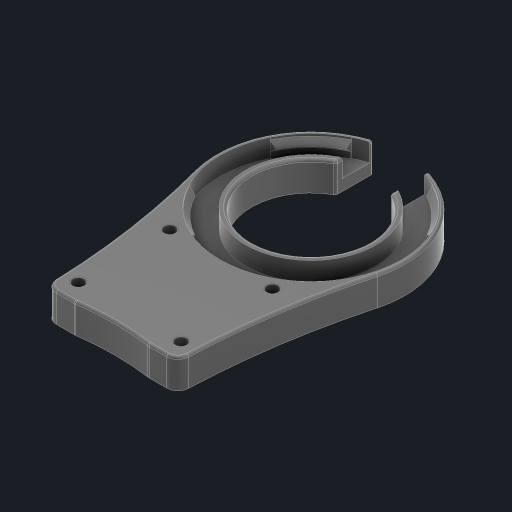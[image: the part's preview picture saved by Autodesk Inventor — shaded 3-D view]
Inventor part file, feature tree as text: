
AUTODESK INVENTOR PART (.ipt)
format: ipt  version: 2023 (Build 270158000, 158)  size: 366,592 bytes
history: native  units: mm
features: extrude x7, fillet x7, sketch x5, draft x2, revolve x1, direct_edit x1, other x1
ambient origin geometry x8: Origin, YZ Plane, XZ Plane, XY Plane, X Axis, Y Axis, Z Axis, Center Point
bodies: Solid1 (feature_tree)
feature tree (24):
  sketch  "Sketch1"  dims[d0=35.5mm d2=49.02mm]
  extrude  "Extrusion1"  Depth=49.02mm
  extrude  "Extrusion2"  Depth=7.0mm TaperAngle=0.0deg
  draft  "FaceDraft1"
  sketch  "Sketch2"  dims[d3=1.2mm d4=7.0mm d5=0.0mm]
  extrude  "Extrusion3"  Depth=0.401426mm
  revolve  "Revolution1"  [1 undecoded]
  extrude  "Extrusion4"  Depth=6.0mm TaperAngle=0.0deg
  direct_edit  "Direct Edit3"
  extrude  "Extrusion6"  Depth=3.1mm
  extrude  "Extrusion7"  Depth=3.0mm
  fillet  "Fillet5"  [1 undecoded]
  fillet  "Fillet6"  [1 undecoded]
  extrude  "Extrusion8"  Depth=23.1mm
  fillet  "Fillet7"  [1 undecoded]
  draft  "FaceDraft3"
  fillet  "Fillet8"  [1 undecoded]
  fillet  "Fillet9"  Radius=14.9mm
  fillet  "Fillet10"  [1 undecoded]
  fillet  "Fillet11"  Radius=3.0mm
  sketch  "Sketch3"  dims[d6=2.0mm d7=0.0mm d8=0.401426mm]
  sketch  "Sketch5"  dims[d22=1.6mm d23=14.9mm]
  sketch  "Sketch6"  dims[d24=3.0mm d25=6.0mm d26=0.0mm d29=3.1mm d30=3.0mm d31=45.0deg d32=90.0deg d33=23.1mm d34=90.0deg d35=0.0mm d36=0.0mm d40=14.9mm d49=-0.127mm d51=3.0mm d52=0.0mm d53=22.0mm d54=22.0mm d55=10.0mm d56=0.0mm d57=0.8mm d58=0.5mm d59=45.0mm d60=8.0mm d62=36.0mm d63=3.0mm d64=0.0mm d65=0.7mm d66=3.2mm d67=24.5mm d68=3.2mm d69=24.9mm d70=1.745329mm d71=70.0mm d72=200.0mm d73=3.0mm d74=0.6mm d75=14.0mm d76=0.0mm]
  other  "Size1"
note: 6 required parameter values undecoded (feature->parameter linkage not recoverable at this tier; creation-order binding heuristic only, values carry confidence <= 0.55)